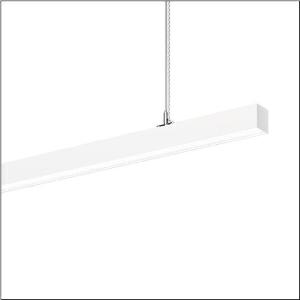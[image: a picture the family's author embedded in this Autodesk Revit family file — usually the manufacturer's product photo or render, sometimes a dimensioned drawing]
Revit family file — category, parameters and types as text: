
# Revit family: silica_r__21_51mx33dc3dwb_1062
name_source: partatom
category: Lighting Fixtures
units: mm (PartAtom-declared; Revit-internal decimal feet)

## family parameters
Cut with Voids When Loaded = No
Host = Face
Light Source = No
Part Type = Normal
Room Calculation Point = No
Round Connector Dimension = Use Diameter
Shared = No

## types (1)
- --- (1 x LED, 14780 lm, 99.5 W, 3000K)
    Apparent Load = 100 VA
    CIE Flux Codes = 78 96 99 55 100
    Color Rendering = 80
    Color Temperature = 3000K
    Default Elevation = 1800 mm
    Description = Silica® 21, office luminaire, primary optical cover: prismatic diffuser, of PMMA, CAT 2 (L<= 3000cd/m²), light emission: direct/indirect distribution, primary light characteristic: symmetric, installation type: suspended mounting, LED, rated luminous flux: 14.780lm, luminous efficacy: 149lm/W, light colour: 830, colour temperature: 3000K, with terminal, 3+2-pole, max. 2.5mm², mains connection: 220..240V, AC, 50/60Hz, rated input power: 99.5W, luminaire housing, of aluminium, traffic white (RAL 9016), length: 3.004mm, width: 53mm, height: 53mm, protection rating (complete): IP20, insulation class (complete): insulation class I (protective earthing), certification: CE, permissible operating ambient temperature: 0..+35°C, standard: EN 50419, packaging unit: 1 piece
    Height = 53 mm
    Lamp = 1 x LED
    Lamp Light Flux = 14780 lm
    Lamp Power = 99.5 W
    Lamp count = 1
    Length = 3004 mm
    Luminous efficacy = 149 lm/W
    Manufacturer = Siteco
    ModVariant = No
    Model = 51MX33DC3DWB
    Mounting Place = Ceiling
    Mounting Type = Pendant
    Number of Poles = 1
    OnlyDefault = Yes
    Power Factor = 1
    Product Name = Silica® 21
    Product group = office luminaire | ceiling pendant
    ProductGroupID = 902
    Protection Class = Protection class I
    Protection Degree = IP 20
    RLX_Detail_Level = 1
    RLX_Emergency_Light_Flux = 0 lm
    RLX_Emergency_Type = 0
    RLX_Emergency_Type_DB = No
    RlxData = <blob elided: 21513 chars, md5=fb105ec2>
    Socket = socket
    Standby Power = 0 W
    System Light Flux = 14780 lm
    System Power = 100 W
    Type Comments = factory setting: luminous flux: 100 % | dim-lin: 254 | 345 mA
    Type Image = l_1335916.jpg
    URL = http://relux.com
    VarID = @adj_087961
    Voltage = 0 V
    Weight = 0.00 kg
    Width = 53 mm

## geometry (parser evidence)
native form markers: Blend x4, Sweep x14
no freeform markers — native parametric forms only
